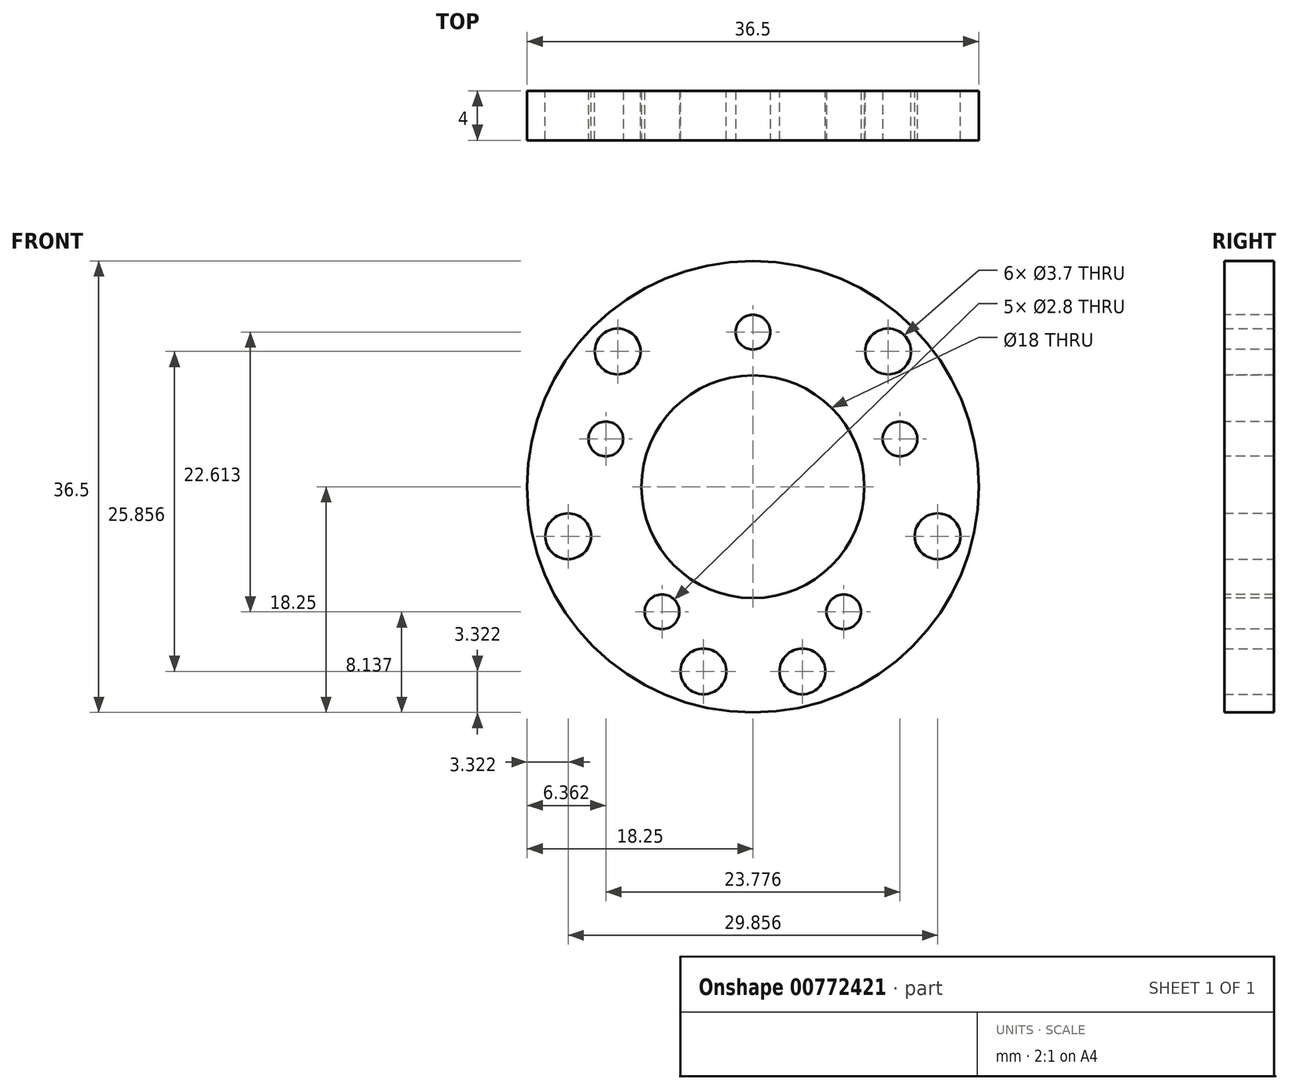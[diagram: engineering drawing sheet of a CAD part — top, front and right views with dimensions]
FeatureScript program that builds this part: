
annotation { "Feature Type Name" : "Feature", "Feature Type Description" : "" }
export const myFeature = defineFeature(function(context is Context, id is Id, definition is map)
    precondition{}
    {
        {
            var Q0;
            Q0=qCreatedBy(makeId("Front.planeOp"),FACE);
            var sketch = newSketch(context, id + "F0", { "sketchPlane" : qUnion([Q0])});
            skCircle(sketch, "E0", {"center": v(0, 0) * mm, "radius": 18.25 * mm});
            skCircle(sketch, "E1", {"center": v(0, 0) * mm, "radius": 9 * mm});
            skCircle(sketch, "E2.cCircle", {"center": v(0, 0) * mm, "radius": 12.5 * mm, "construction": true});
            skLineSegment(sketch, "E2.0", {"start": v(0, 12.5) * mm, "end": v(11.89, 3.86) * mm, "construction": true});
            skLineSegment(sketch, "E2.1", {"start": v(11.89, 3.86) * mm, "end": v(7.35, -10.11) * mm, "construction": true});
            skLineSegment(sketch, "E2.2", {"start": v(7.35, -10.11) * mm, "end": v(-7.35, -10.11) * mm, "construction": true});
            skLineSegment(sketch, "E2.3", {"start": v(-7.35, -10.11) * mm, "end": v(-11.89, 3.86) * mm, "construction": true});
            skLineSegment(sketch, "E2.4", {"start": v(-11.89, 3.86) * mm, "end": v(0, 12.5) * mm, "construction": true});
            skCircle(sketch, "E3", {"center": v(0, 12.5) * mm, "radius": 1.4 * mm});
            skCircle(sketch, "E4", {"center": v(11.89, 3.86) * mm, "radius": 1.4 * mm});
            skCircle(sketch, "E5", {"center": v(7.35, -10.11) * mm, "radius": 1.4 * mm});
            skCircle(sketch, "E6", {"center": v(-7.35, -10.11) * mm, "radius": 1.4 * mm});
            skCircle(sketch, "E7", {"center": v(-11.89, 3.86) * mm, "radius": 1.4 * mm});
            skSolve(sketch);
        }
        {
            var Q0;
            Q0=makeQuery(id+"F0.imprint","IMPRINT",FACE,{"disambiguationData":[TD([[makeQuery(id+"F0.imprint","IMPRINT",EDGE,{"derivedFrom":sQuery(id+"F0.wireOp",EDGE,"E0")}),1.0]])]});
            extrude(context, id + "F1", {"entities" : qUnion([Q0]), "oppositeDirection" : true, "depth" : 4 * mm, "offsetDistance" : 25 * mm});
        }
        {
            var Q0;
            Q0=makeQuery(id+"F1.opExtrude","CAP_FACE",FACE,{"disambiguationData":[OSD([sQuery(id+"F0.wireOp",EDGE,"E0"),sQuery(id+"F0.wireOp",EDGE,"E1"),sQuery(id+"F0.wireOp",EDGE,"E3"),sQuery(id+"F0.wireOp",EDGE,"E4"),sQuery(id+"F0.wireOp",EDGE,"E5"),sQuery(id+"F0.wireOp",EDGE,"E6"),sQuery(id+"F0.wireOp",EDGE,"E7")])],"isStart":false});
            var sketch = newSketch(context, id + "F2", { "sketchPlane" : qUnion([Q0])});
            skCircle(sketch, "E8.cCircle", {"center": v(0, 0) * mm, "radius": 15.45 * mm, "construction": true});
            skLineSegment(sketch, "E8.0", {"start": v(4, 14.93) * mm, "end": v(10.93, 10.93) * mm, "construction": true});
            skLineSegment(sketch, "E8.1", {"start": v(10.93, 10.93) * mm, "end": v(14.93, 4) * mm, "construction": true});
            skLineSegment(sketch, "E8.2", {"start": v(14.93, 4) * mm, "end": v(14.93, -4) * mm, "construction": true});
            skLineSegment(sketch, "E8.3", {"start": v(14.93, -4) * mm, "end": v(10.93, -10.93) * mm, "construction": true});
            skLineSegment(sketch, "E8.4", {"start": v(10.93, -10.93) * mm, "end": v(4, -14.93) * mm, "construction": true});
            skLineSegment(sketch, "E8.5", {"start": v(4, -14.93) * mm, "end": v(-4, -14.93) * mm, "construction": true});
            skLineSegment(sketch, "E8.6", {"start": v(-4, -14.93) * mm, "end": v(-10.93, -10.93) * mm, "construction": true});
            skLineSegment(sketch, "E8.7", {"start": v(-10.93, -10.93) * mm, "end": v(-14.93, -4) * mm, "construction": true});
            skLineSegment(sketch, "E8.8", {"start": v(-14.93, -4) * mm, "end": v(-14.93, 4) * mm, "construction": true});
            skLineSegment(sketch, "E8.9", {"start": v(-14.93, 4) * mm, "end": v(-10.93, 10.93) * mm, "construction": true});
            skLineSegment(sketch, "E8.10", {"start": v(-10.93, 10.93) * mm, "end": v(-4, 14.93) * mm, "construction": true});
            skLineSegment(sketch, "E8.11", {"start": v(-4, 14.93) * mm, "end": v(4, 14.93) * mm, "construction": true});
            skLineSegment(sketch, "E9", {"start": v(0, 0) * mm, "end": v(0, -14.93) * mm, "construction": true});
            skCircle(sketch, "E10", {"center": v(-10.93, 10.93) * mm, "radius": 1.85 * mm});
            skCircle(sketch, "E11", {"center": v(10.93, 10.93) * mm, "radius": 1.85 * mm});
            skCircle(sketch, "E12", {"center": v(14.93, -4) * mm, "radius": 1.85 * mm});
            skCircle(sketch, "E13", {"center": v(4, -14.93) * mm, "radius": 1.85 * mm});
            skCircle(sketch, "E14", {"center": v(-4, -14.93) * mm, "radius": 1.85 * mm});
            skCircle(sketch, "E15", {"center": v(-14.93, -4) * mm, "radius": 1.85 * mm});
            skSolve(sketch);
        }
        {
            var Q0;
            Q0=makeQuery(id+"F2.imprint","IMPRINT",FACE,{"disambiguationData":[TD([[makeQuery(id+"F2.imprint","IMPRINT",EDGE,{"derivedFrom":sQuery(id+"F2.wireOp",EDGE,"E15")}),1.0]])]});
            var Q1;
            Q1=makeQuery(id+"F2.imprint","IMPRINT",FACE,{"disambiguationData":[TD([[makeQuery(id+"F2.imprint","IMPRINT",EDGE,{"derivedFrom":sQuery(id+"F2.wireOp",EDGE,"E10")}),1.0]])]});
            var Q2;
            Q2=makeQuery(id+"F2.imprint","IMPRINT",FACE,{"disambiguationData":[TD([[makeQuery(id+"F2.imprint","IMPRINT",EDGE,{"derivedFrom":sQuery(id+"F2.wireOp",EDGE,"E12")}),1.0]])]});
            var Q3;
            Q3=makeQuery(id+"F2.imprint","IMPRINT",FACE,{"disambiguationData":[TD([[makeQuery(id+"F2.imprint","IMPRINT",EDGE,{"derivedFrom":sQuery(id+"F2.wireOp",EDGE,"E11")}),1.0]])]});
            var Q4;
            Q4=makeQuery(id+"F2.imprint","IMPRINT",FACE,{"disambiguationData":[TD([[makeQuery(id+"F2.imprint","IMPRINT",EDGE,{"derivedFrom":sQuery(id+"F2.wireOp",EDGE,"E13")}),1.0]])]});
            var Q5;
            Q5=makeQuery(id+"F2.imprint","IMPRINT",FACE,{"disambiguationData":[TD([[makeQuery(id+"F2.imprint","IMPRINT",EDGE,{"derivedFrom":sQuery(id+"F2.wireOp",EDGE,"E14")}),1.0]])]});
            extrude(context, id + "F3", {"entities" : qUnion([Q0, Q1, Q2, Q3, Q4, Q5]), "operationType" : NewBodyOperationType.REMOVE, "oppositeDirection" : true, "depth" : 25 * mm, "offsetDistance" : 25 * mm});
        }
    });
